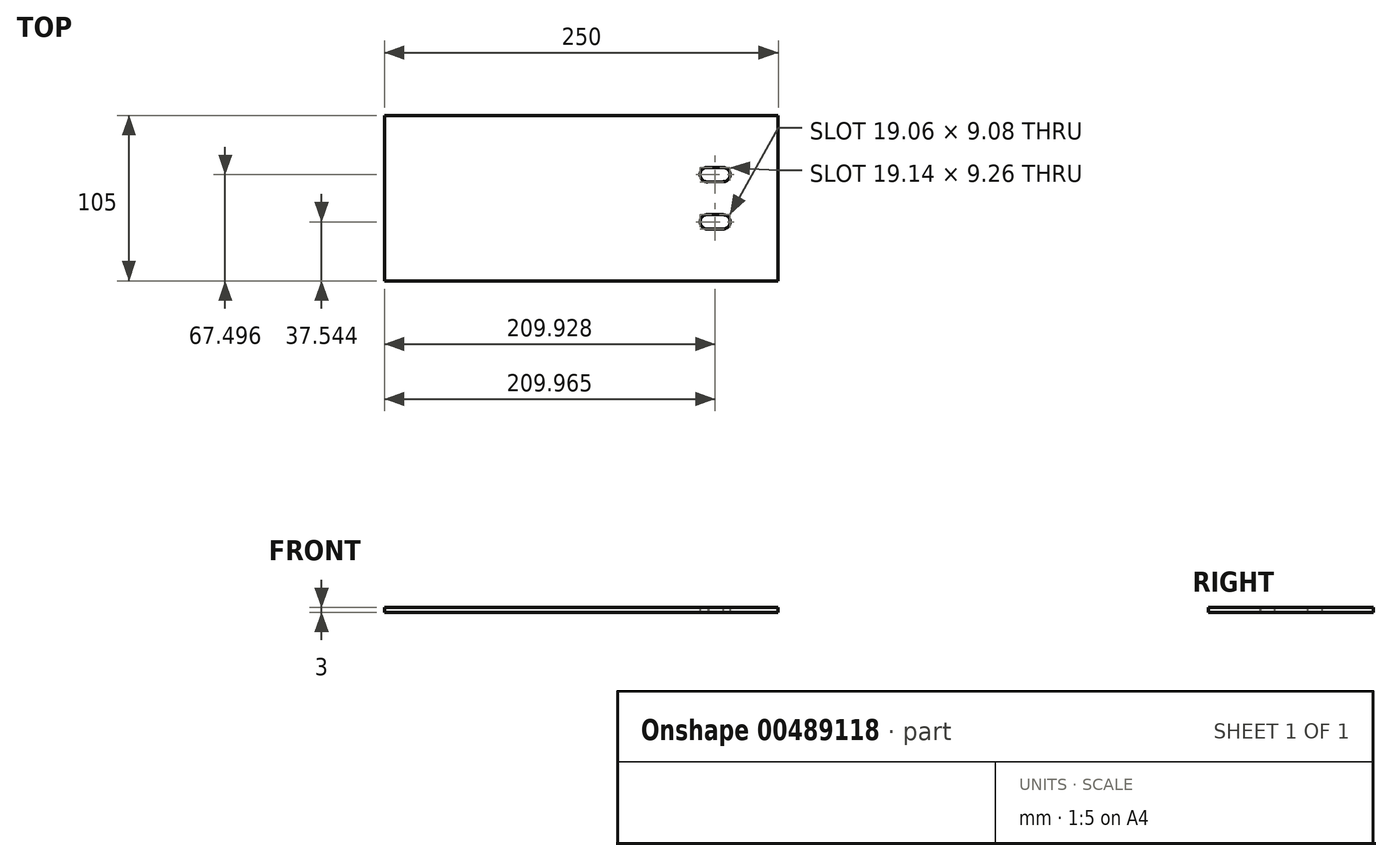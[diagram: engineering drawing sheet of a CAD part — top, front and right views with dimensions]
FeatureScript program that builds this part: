
annotation { "Feature Type Name" : "Feature", "Feature Type Description" : "" }
export const myFeature = defineFeature(function(context is Context, id is Id, definition is map)
    precondition{}
    {
        {
            var Q0;
            Q0=qCreatedBy(makeId("Top.planeOp"),FACE);
            var sketch = newSketch(context, id + "F0", { "sketchPlane" : qUnion([Q0])});
            skLineSegment(sketch, "E0.bottom", {"start": v(-127.84, 47.71) * mm, "end": v(122.16, 47.71) * mm});
            skLineSegment(sketch, "E0.top", {"start": v(-127.84, -57.29) * mm, "end": v(122.16, -57.29) * mm});
            skLineSegment(sketch, "E0.left", {"start": v(-127.84, 47.71) * mm, "end": v(-127.84, -57.29) * mm});
            skLineSegment(sketch, "E0.right", {"start": v(122.16, 47.71) * mm, "end": v(122.16, -57.29) * mm});
            skCircle(sketch, "E1", {"center": v(87.16, 10.21) * mm, "radius": 4.5 * mm});
            skCircle(sketch, "E2", {"center": v(87.16, -19.79) * mm, "radius": 4.5 * mm});
            skCircle(sketch, "E3", {"center": v(77.16, 10.21) * mm, "radius": 4.64 * mm});
            skCircle(sketch, "E4", {"center": v(77.16, -19.79) * mm, "radius": 4.58 * mm});
            skLineSegment(sketch, "E5", {"start": v(76.9, 14.85) * mm, "end": v(87.22, 14.71) * mm});
            skLineSegment(sketch, "E6", {"start": v(77.25, 5.57) * mm, "end": v(87.22, 5.71) * mm});
            skLineSegment(sketch, "E7", {"start": v(87, -15.29) * mm, "end": v(77.2, -15.2) * mm});
            skLineSegment(sketch, "E8", {"start": v(87.17, -24.29) * mm, "end": v(78.02, -24.29) * mm});
            skSolve(sketch);
        }
        {
            var Q0;
            Q0=makeQuery(id+"F0.imprint","IMPRINT",FACE,{"disambiguationData":[TD([[makeQuery(id+"F0.imprint","IMPRINT",EDGE,{"derivedFrom":sQuery(id+"F0.wireOp",EDGE,"E0.bottom")}),-1.0]])]});
            extrude(context, id + "F1", {"entities" : qUnion([Q0]), "depth" : 3 * mm});
        }
        {
            var Q0;
            Q0 = qSketchRegion(id + "F0", true);
            extrude(context, id + "F2", {"entities" : qUnion([Q0]), "operationType" : NewBodyOperationType.REMOVE, "oppositeDirection" : true, "depth" : 3 * mm, "offsetDistance" : 25 * mm});
        }
    });
